# Revit family: PRD_FrankeWS_Hrdrrs_HoodHairDryer_F5DR2001-2005
name_source: partatom
category: Specialty Equipment
revit_build: Autodesk Revit 2018 (Build: 20190510_1515(x64)
units: mm (PartAtom-declared; Revit-internal decimal feet)

## family parameters
Cut with Voids When Loaded = No
Host = Face
OmniClass Number = 23.40.20.21.14
OmniClass Title = Hand and Hair Dryers
Part Type = Normal
Room Calculation Point = No
Round Connector Dimension = Use Diameter
Shared = No

## types (5) — shared parameters
AirVelocity = 8 m/s
ApparentLoad = 0 VA
AssetType = Fixed
BlowerOutput = 190 m3/h
BodyMaterial = PRD_AR_SyntheticLightGrey
Category = Pr_40_70_62_36, Hairdryers
ConnectionVoltage = 230 V AC, 50-60 Hz
Default Elevation = 1800 mm  [stored 5.90551 ft]
DurationUnit = year
Features = thermoplastic material, 4 air outlets
GrossWeight = 5.80 kg
HeatingPower = 1200.00 watt
IP_Code = IP23
IfcExportAs = IfcElectricApplianceType
IfcExportType = USERDEFINED
InputSupplyVoltageHz = 50.00 hertz
InputSupplyVoltageV = 230.00 volt
InsideMaterial = PRD_AR_Black
LoadClassification = Other
Manufacturer = KWC Group AG
ManufacturerName = KWC Group AG
ManufacturerURL = www.kwc.com
Material = Synthetic
MotorPower = 55.00 watt
NBSDescription = Hair dryers
NBSReference = 45-35-72/335
NetWeight = 5.20 kg
NoiseLevel = 66 db (A)
NominalDepth = 307 mm  [stored 1.00722 ft]
NominalFrequencyRange = 50 Hz
NominalHeight = 331 mm  [stored 1.08596 ft]
NominalWidth = 280 mm  [stored 0.918635 ft]
PowerFactor = 1
ProductInformation = https://pim.kwc.com
ProtectiveSystemIP = IP23
RatedCurrent = 0
RatedVoltage = 230 V
Size = 280 x 331 x 307 mm (W x H x D)
TailorMade = No
TotalPower = 1300.00 watt
TypeOfFixing = Screw
TypeOfMounting = Wall mounting
TypeOfOperation = Sensor operation
URL = www.kwc.com
Uniclass2015Code = Pr_40_70_62_36
Uniclass2015Title = Hairdryers
Uniclass2015Version = Products v1.17
Version = 1
Voltage = 230 V
WarrantyDurationUnit = year

## per-type parameters (varying)
| type | BIMObjectName | Color | ColorMaterial | Description | ModelNumber | Name |
| F5DR2001 | PRD_AR_Hairdryers_HoodHairDryer_F5DR2001 | White | PRD_AR_SyntheticWhite | F5 hood hair dryer for wall mounting, opto-electronically controlled for touch-free activation, integrated ion technology, brushless and maintenance-free EC motor. Sensor range and safety switch-off for permanent reflexion adjustable using optional bidirectional remote control. Made of thermoplastic material, housing and mounting in light grey, drying recess in white, with 4 air outlets for even hot air distribution. | 2030050305 | Hood Hair Dryer F5DR2001 |
| F5DR2002 | PRD_AR_Hairdryers_HoodHairDryer_F5DR2002 | Basalt grey | PRD_AR_SyntheticBasaltGrey | F5 hood hair dryer for wall mounting, opto-electronically controlled for touch-free activation, integrated ion technology, brushless and maintenance-free EC motor. Sensor range and safety switch-off for permanent reflexion adjustable using optional bidirectional remote control. Made of thermoplastic material, housing and mounting in light grey, drying recess in basalt grey, with 4 air outlets for even hot air distribution. | 2030052323 | Hood Hair Dryer F5DR2002 |
| F5DR2003 | PRD_AR_Hairdryers_HoodHairDryer_F5DR2003 | Pearl gentian blue | PRD_AR_SyntheticPearlGentianBlue | F5 hood hair dryer for wall mounting, opto-electronically controlled for touch-free activation, integrated ion technology, brushless and maintenance-free EC motor. Sensor range and safety switch-off for permanent reflexion adjustable using optional bidirectional remote control. Made of thermoplastic material, housing and mounting in light grey, drying recess in pearl gentian blue, with 4 air outlets for even hot air distribution. | 2030052324 | Hood Hair Dryer F5DR2003 |
| F5DR2004 | PRD_AR_Hairdryers_HoodHairDryer_F5DR2004 | Lemon yellow | PRD_AR_SyntheticLemonYellow | F5 hood hair dryer for wall mounting, opto-electronically controlled for touch-free activation, integrated ion technology, brushless and maintenance-free EC motor. Sensor range and safety switch-off for permanent reflexion adjustable using optional bidirectional remote control. Made of thermoplastic material, housing and mounting in light grey, drying recess in lemon yellow, with 4 air outlets for even hot air distribution. | 2030052327 | Hood Hair Dryer F5DR2004 |
| F5DR2005 | PRD_AR_Hairdryers_HoodHairDryer_F5DR2005 | Signal red | PRD_AR_SyntheticSignalRed | F5 hood hair dryer for wall mounting, opto-electronically controlled for touch-free activation, integrated ion technology, brushless and maintenance-free EC motor. Sensor range and safety switch-off for permanent reflexion adjustable using optional bidirectional remote control. Made of thermoplastic material, housing and mounting in light grey, drying recess in signal red, with 4 air outlets for even hot air distribution. | 2030052328 | Hood Hair Dryer F5DR2005 |

note: column(s) folded — value = type name in every type: Model, ModelReference

note: [stored X ft] marks values corroborated as IEEE doubles in the binary element streams (Revit-internal decimal feet)

## geometry (parser evidence)
native form markers: Sweep x4
no freeform markers — native parametric forms only
